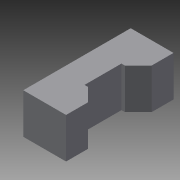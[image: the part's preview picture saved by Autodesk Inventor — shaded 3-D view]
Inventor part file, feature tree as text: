
AUTODESK INVENTOR PART (.ipt)
format: ipt  version: 2015 (Build 190159000, 159)  size: 98,304 bytes
history: native  units: mm
features: extrude x2, sketch x2, projected_geometry x1
ambient origin geometry x8: Origin, YZ Plane, XZ Plane, XY Plane, X Axis, Y Axis, Z Axis, Center Point
bodies: Solid1 (feature_tree)
feature tree (5):
  extrude  "Extrusion1"  Depth=6.35mm
  extrude  "Extrusion3"  Depth=12.0mm TaperAngle=0.0deg
  sketch  "Sketch1"  dims[d0=1.0mm d1=6.35mm]
  sketch  "Sketch3"  dims[d2=8.75mm d3=12.0mm d4=0.0mm d8=2.54mm d9=9.5mm d10=7.62mm d11=5.0mm d12=0.0mm d13=135.0deg d14=135.0deg d15=11.0mm d16=12.75mm d17=32.0mm]
  projected_geometry  "Projected Loop1"
